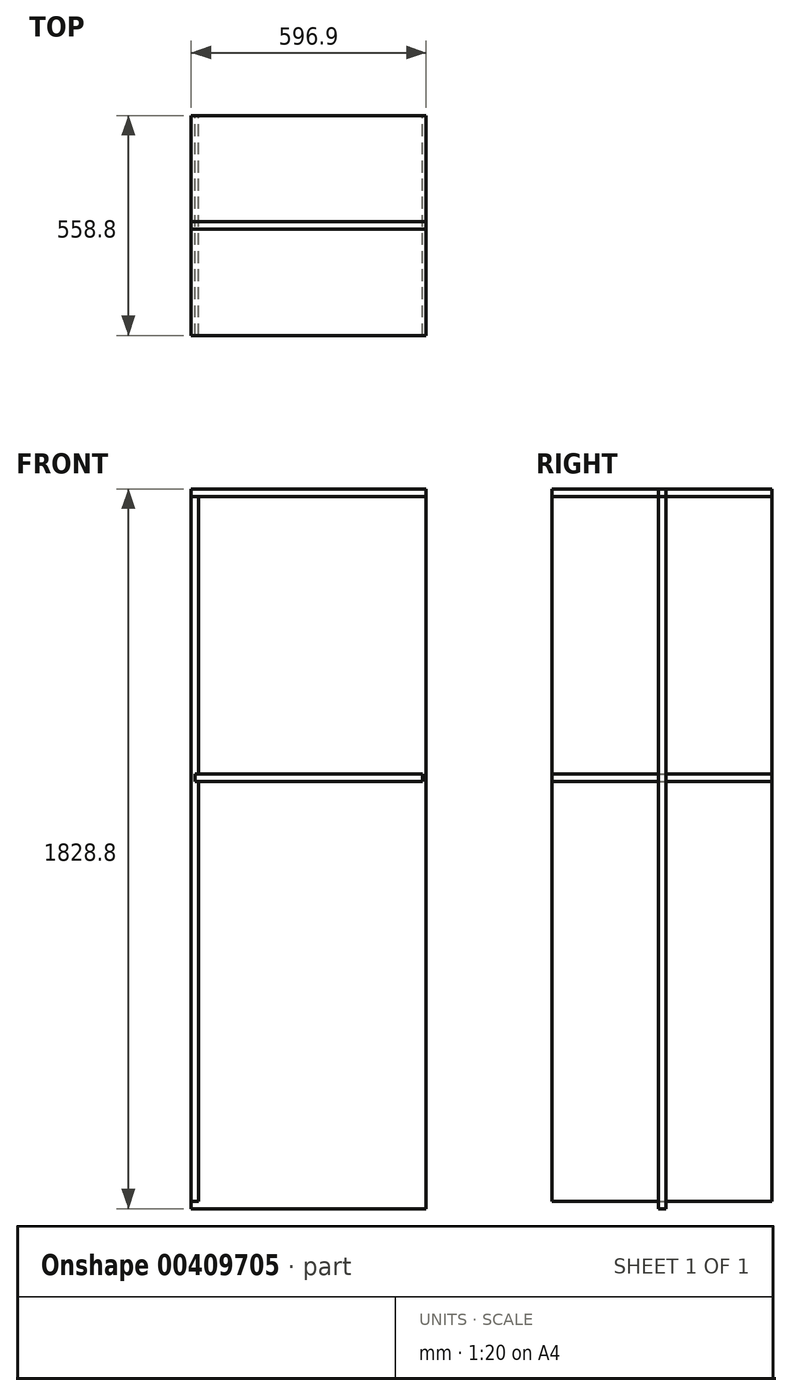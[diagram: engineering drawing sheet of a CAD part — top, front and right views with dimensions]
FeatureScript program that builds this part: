
annotation { "Feature Type Name" : "Feature", "Feature Type Description" : "" }
export const myFeature = defineFeature(function(context is Context, id is Id, definition is map)
    precondition{}
    {
        {
            assignVariable(context, id + "F0", {"name" : "MaterialThickness", "anyValue" : 19.05 * mm});
        }
        {
            var Q0;
            Q0=qCreatedBy(makeId("Front.planeOp"),FACE);
            var sketch = newSketch(context, id + "F1", { "sketchPlane" : qUnion([Q0])});
            skLineSegment(sketch, "E0.bottom", {"start": v(-298.45, 895.35) * mm, "end": v(298.45, 895.35) * mm});
            skLineSegment(sketch, "E0.top", {"start": v(-298.45, -895.35) * mm, "end": v(298.45, -895.35) * mm});
            skLineSegment(sketch, "E0.left", {"start": v(-298.45, 895.35) * mm, "end": v(-298.45, -895.35) * mm});
            skLineSegment(sketch, "E0.right", {"start": v(298.45, 895.35) * mm, "end": v(298.45, -895.35) * mm});
            skPoint(sketch, "E0.middle", {"position": v(0, 0) * mm});
            skLineSegment(sketch, "E1", {"start": v(-279.4, 895.35) * mm, "end": v(-279.4, -895.35) * mm});
            skLineSegment(sketch, "E2.MirrorCS", {"start": v(279.4, 895.35) * mm, "end": v(279.4, -895.35) * mm});
            skLineSegment(sketch, "E3.bottom", {"start": v(-288.93, 190.5) * mm, "end": v(288.93, 190.5) * mm});
            skLineSegment(sketch, "E3.top", {"start": v(-288.93, 171.45) * mm, "end": v(288.93, 171.45) * mm});
            skLineSegment(sketch, "E3.left", {"start": v(-288.93, 190.5) * mm, "end": v(-288.93, 171.45) * mm});
            skLineSegment(sketch, "E3.right", {"start": v(288.93, 190.5) * mm, "end": v(288.93, 171.45) * mm});
            skPoint(sketch, "E3.middle", {"position": v(0, 180.98) * mm});
            skLineSegment(sketch, "E4", {"start": v(-298.45, -895.35) * mm, "end": v(-298.45, -914.4) * mm});
            skLineSegment(sketch, "E5", {"start": v(-298.45, -914.4) * mm, "end": v(298.45, -914.4) * mm});
            skLineSegment(sketch, "E6", {"start": v(298.45, -914.4) * mm, "end": v(298.45, -895.35) * mm});
            skLineSegment(sketch, "E7.MirrorCS", {"start": v(-298.45, 895.35) * mm, "end": v(-298.45, 914.4) * mm});
            skLineSegment(sketch, "E8.MirrorCS", {"start": v(-298.45, 914.4) * mm, "end": v(298.45, 914.4) * mm});
            skLineSegment(sketch, "E9.MirrorCS", {"start": v(298.45, 914.4) * mm, "end": v(298.45, 895.35) * mm});
            skSolve(sketch);
        }
        {
            var Q0;
            {var subQ0=sQuery(id+"F1.wireOp",EDGE,"E0.left");Q0=makeQuery(id+"F1.imprint","IMPRINT",FACE,{"disambiguationData":[TD([[makeQuery(id+"F1.imprint","IMPRINT",EDGE,{"derivedFrom":subQ0}),1.0]])]});}
            extrude(context, id + "F2", {"entities" : qUnion([Q0]), "endBound" : BoundingType.SYMMETRIC, "depth" : 558.8 * mm});
        }
        {
            var Q0;
            {var subQ4=sQuery(id+"F1.wireOp",EDGE,"E7.MirrorCS");Q0=makeQuery(id+"F1.imprint","IMPRINT",FACE,{"disambiguationData":[TD([[makeQuery(id+"F1.imprint","IMPRINT",EDGE,{"derivedFrom":subQ4}),-1.0]])]});}
            var Q1;
            Q1=makeQuery(id+"F2.opExtrude","CAP_FACE",FACE,{"disambiguationData":[OSD([sQuery(id+"F1.wireOp",EDGE,"E0.bottom"),sQuery(id+"F1.wireOp",EDGE,"E0.top"),sQuery(id+"F1.wireOp",EDGE,"E0.left"),sQuery(id+"F1.wireOp",EDGE,"E1"),sQuery(id+"F1.wireOp",EDGE,"E3.bottom"),sQuery(id+"F1.wireOp",EDGE,"E3.top"),sQuery(id+"F1.wireOp",EDGE,"E3.left")])],"isStart":false});
            var Q2;
            Q2=makeQuery(id+"F2.opExtrude","CAP_FACE",FACE,{"disambiguationData":[OSD([sQuery(id+"F1.wireOp",EDGE,"E0.bottom"),sQuery(id+"F1.wireOp",EDGE,"E0.top"),sQuery(id+"F1.wireOp",EDGE,"E0.left"),sQuery(id+"F1.wireOp",EDGE,"E1"),sQuery(id+"F1.wireOp",EDGE,"E3.bottom"),sQuery(id+"F1.wireOp",EDGE,"E3.top"),sQuery(id+"F1.wireOp",EDGE,"E3.left")])],"isStart":true});
            extrude(context, id + "F3", {"entities" : qUnion([Q0]), "endBound" : BoundingType.UP_TO_SURFACE, "endBoundEntityFace" : qUnion([Q1]), "depth" : 25.4 * mm, "hasSecondDirection" : true, "secondDirectionBound" : SecondDirectionBoundingType.UP_TO_SURFACE, "secondDirectionOppositeDirection" : true, "secondDirectionBoundEntityFace" : qUnion([Q2]), "secondDirectionDepth" : 25.4 * mm});
        }
        {
            var Q0;
            {var subQ0=sQuery(id+"F1.wireOp",EDGE,"E3.bottom");var subQ1=sQuery(id+"F1.wireOp",EDGE,"E1");var subQ2=makeQuery(id+"F1.imprint","INTERSECT",VERTEX,{"derivedFrom":[subQ1,subQ0]});Q0=makeQuery(id+"F1.imprint","IMPRINT",FACE,{"disambiguationData":[TD([[makeQuery(id+"F1.imprint","IMPRINT",EDGE,{"disambiguationData":[TD([[subQ2,-1.0]])],"derivedFrom":subQ1}),1.0]])]});}
            var Q1;
            {var subQ5=sQuery(id+"F1.wireOp",EDGE,"E3.left");Q1=makeQuery(id+"F1.imprint","IMPRINT",FACE,{"disambiguationData":[TD([[makeQuery(id+"F1.imprint","IMPRINT",EDGE,{"derivedFrom":subQ5}),1.0]])]});}
            var Q2;
            {var subQ5=sQuery(id+"F1.wireOp",EDGE,"E3.right");Q2=makeQuery(id+"F1.imprint","IMPRINT",FACE,{"disambiguationData":[TD([[makeQuery(id+"F1.imprint","IMPRINT",EDGE,{"derivedFrom":subQ5}),-1.0]])]});}
            var Q3;
            Q3=makeQuery(id+"F2.opExtrude","CAP_FACE",FACE,{"disambiguationData":[OSD([sQuery(id+"F1.wireOp",EDGE,"E0.bottom"),sQuery(id+"F1.wireOp",EDGE,"E0.top"),sQuery(id+"F1.wireOp",EDGE,"E0.left"),sQuery(id+"F1.wireOp",EDGE,"E1"),sQuery(id+"F1.wireOp",EDGE,"E3.bottom"),sQuery(id+"F1.wireOp",EDGE,"E3.top"),sQuery(id+"F1.wireOp",EDGE,"E3.left")])],"isStart":false});
            var Q4;
            Q4=makeQuery(id+"F2.opExtrude","CAP_FACE",FACE,{"disambiguationData":[OSD([sQuery(id+"F1.wireOp",EDGE,"E0.bottom"),sQuery(id+"F1.wireOp",EDGE,"E0.top"),sQuery(id+"F1.wireOp",EDGE,"E0.left"),sQuery(id+"F1.wireOp",EDGE,"E1"),sQuery(id+"F1.wireOp",EDGE,"E3.bottom"),sQuery(id+"F1.wireOp",EDGE,"E3.top"),sQuery(id+"F1.wireOp",EDGE,"E3.left")])],"isStart":true});
            extrude(context, id + "F4", {"entities" : qUnion([Q0, Q1, Q2]), "endBound" : BoundingType.UP_TO_SURFACE, "endBoundEntityFace" : qUnion([Q3]), "depth" : 25.4 * mm, "hasSecondDirection" : true, "secondDirectionBound" : SecondDirectionBoundingType.UP_TO_SURFACE, "secondDirectionOppositeDirection" : true, "secondDirectionBoundEntityFace" : qUnion([Q4]), "secondDirectionDepth" : 25.4 * mm});
        }
        {
            var Q0;
            {var subQ5=sQuery(id+"F1.wireOp",EDGE,"E3.right");Q0=makeQuery(id+"F1.imprint","IMPRINT",FACE,{"disambiguationData":[TD([[makeQuery(id+"F1.imprint","IMPRINT",EDGE,{"derivedFrom":subQ5}),-1.0]])]});}
            var Q1;
            {var subQ0=sQuery(id+"F1.wireOp",EDGE,"E3.bottom");var subQ1=sQuery(id+"F1.wireOp",EDGE,"E1");var subQ2=makeQuery(id+"F1.imprint","INTERSECT",VERTEX,{"derivedFrom":[subQ1,subQ0]});Q1=makeQuery(id+"F1.imprint","IMPRINT",FACE,{"disambiguationData":[TD([[makeQuery(id+"F1.imprint","IMPRINT",EDGE,{"disambiguationData":[TD([[subQ2,-1.0]])],"derivedFrom":subQ1}),1.0]])]});}
            var Q2;
            {var subQ5=sQuery(id+"F1.wireOp",EDGE,"E3.left");Q2=makeQuery(id+"F1.imprint","IMPRINT",FACE,{"disambiguationData":[TD([[makeQuery(id+"F1.imprint","IMPRINT",EDGE,{"derivedFrom":subQ5}),1.0]])]});}
            var Q3;
            {var subQ0=sQuery(id+"F1.wireOp",EDGE,"E4");Q3=makeQuery(id+"F1.imprint","IMPRINT",FACE,{"disambiguationData":[TD([[makeQuery(id+"F1.imprint","IMPRINT",EDGE,{"derivedFrom":subQ0}),1.0]])]});}
            var Q4;
            {var subQ4=sQuery(id+"F1.wireOp",EDGE,"E7.MirrorCS");Q4=makeQuery(id+"F1.imprint","IMPRINT",FACE,{"disambiguationData":[TD([[makeQuery(id+"F1.imprint","IMPRINT",EDGE,{"derivedFrom":subQ4}),-1.0]])]});}
            var Q5;
            {var subQ0=sQuery(id+"F1.wireOp",EDGE,"E0.left");Q5=makeQuery(id+"F1.imprint","IMPRINT",FACE,{"disambiguationData":[TD([[makeQuery(id+"F1.imprint","IMPRINT",EDGE,{"derivedFrom":subQ0}),1.0]])]});}
            var Q6;
            {var subQ5=sQuery(id+"F1.wireOp",EDGE,"E0.right");Q6=makeQuery(id+"F1.imprint","IMPRINT",FACE,{"disambiguationData":[TD([[makeQuery(id+"F1.imprint","IMPRINT",EDGE,{"derivedFrom":subQ5}),-1.0]])]});}
            var Q7;
            {var subQ0=sQuery(id+"F1.wireOp",EDGE,"E1");var subQ1=sQuery(id+"F1.wireOp",EDGE,"E0.top");var subQ2=makeQuery(id+"F1.imprint","INTERSECT",VERTEX,{"derivedFrom":[subQ1,subQ0]});Q7=makeQuery(id+"F1.imprint","IMPRINT",FACE,{"disambiguationData":[TD([[makeQuery(id+"F1.imprint","IMPRINT",EDGE,{"disambiguationData":[TD([[subQ2,-1.0]])],"derivedFrom":subQ1}),1.0]])]});}
            var Q8;
            {var subQ0=sQuery(id+"F1.wireOp",EDGE,"E1");var subQ1=sQuery(id+"F1.wireOp",EDGE,"E0.bottom");var subQ2=makeQuery(id+"F1.imprint","INTERSECT",VERTEX,{"derivedFrom":[subQ1,subQ0]});Q8=makeQuery(id+"F1.imprint","IMPRINT",FACE,{"disambiguationData":[TD([[makeQuery(id+"F1.imprint","IMPRINT",EDGE,{"disambiguationData":[TD([[subQ2,-1.0]])],"derivedFrom":subQ1}),-1.0]])]});}
            extrude(context, id + "F5", {"entities" : qUnion([Q0, Q1, Q2, Q3, Q4, Q5, Q6, Q7, Q8]), "endBound" : BoundingType.SYMMETRIC, "depth" : getVariable(context, 'MaterialThickness')});
        }
    });
